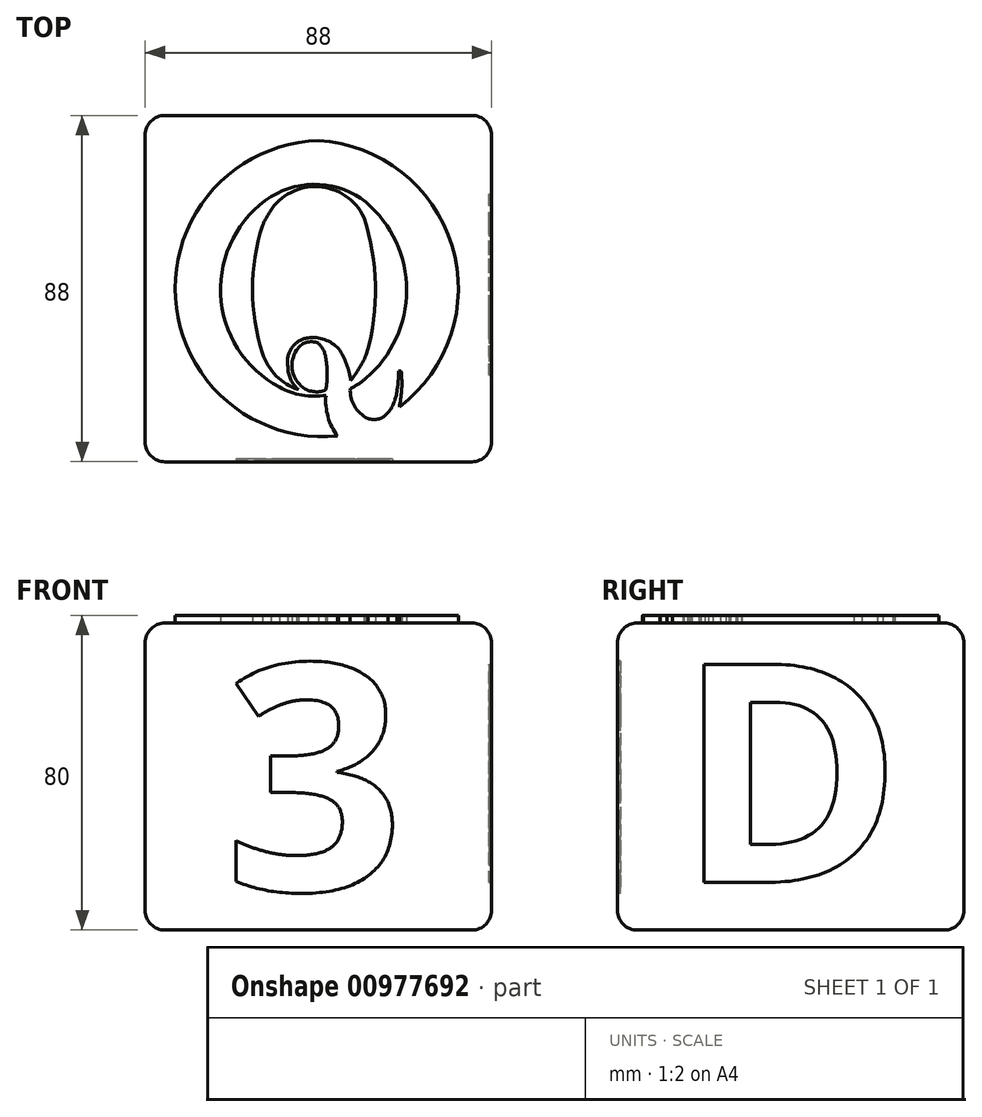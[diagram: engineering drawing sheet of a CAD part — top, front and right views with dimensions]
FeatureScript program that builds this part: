
annotation { "Feature Type Name" : "Feature", "Feature Type Description" : "" }
export const myFeature = defineFeature(function(context is Context, id is Id, definition is map)
    precondition{}
    {
        {
            var Q0;
            Q0=qCreatedBy(makeId("Top.planeOp"),FACE);
            var sketch = newSketch(context, id + "F0", { "sketchPlane" : qUnion([Q0])});
            skPoint(sketch, "E0.first.point", {"position": v(-8.97, 42.4) * mm});
            skPoint(sketch, "E0.second.point", {"position": v(4.84, -31.38) * mm});
            skPoint(sketch, "E0.third.point", {"position": v(40.23, 13.72) * mm});
            skArc(sketch, "E1", {"start": v(0, 43.7) * mm, "mid": v(-36.34, 3.66) * mm, "end": v(4.84, -31.38) * mm});
            skArc(sketch, "E2", {"start": v(20.57, -24) * mm, "mid": v(33.91, 17.02) * mm, "end": v(0, 43.7) * mm});
            skArc(sketch, "E3", {"start": v(-12, 29.47) * mm, "mid": v(-24.84, 4.65) * mm, "end": v(-9.87, -18.96) * mm});
            skArc(sketch, "E4", {"start": v(12.09, 28.05) * mm, "mid": v(0.27, 32.56) * mm, "end": v(-12, 29.47) * mm});
            skArc(sketch, "E5", {"start": v(12.09, -16.68) * mm, "mid": v(22.4, 5.68) * mm, "end": v(12.09, 28.05) * mm});
            skArc(sketch, "E6", {"start": v(8.11, -19.25) * mm, "mid": v(10.22, -18.15) * mm, "end": v(12.09, -16.68) * mm});
            skArc(sketch, "E7", {"start": v(-9.87, -18.96) * mm, "mid": v(-4.16, -21) * mm, "end": v(1.9, -21.05) * mm});
            skArc(sketch, "E8", {"start": v(1.9, -21.05) * mm, "mid": v(2.44, -26.48) * mm, "end": v(4.84, -31.38) * mm});
            skArc(sketch, "E9", {"start": v(8.11, -19.25) * mm, "mid": v(9.16, -23.77) * mm, "end": v(12.57, -26.92) * mm});
            skArc(sketch, "E10", {"start": v(12.57, -26.92) * mm, "mid": v(15.38, -27) * mm, "end": v(17.7, -25.42) * mm});
            skArc(sketch, "E11", {"start": v(17.7, -25.42) * mm, "mid": v(19.27, -22.75) * mm, "end": v(19.99, -19.74) * mm});
            skArc(sketch, "E12", {"start": v(19.99, -19.74) * mm, "mid": v(20.3, -17.3) * mm, "end": v(20.33, -14.85) * mm});
            skLineSegment(sketch, "E13", {"start": v(20.33, -14.85) * mm, "end": v(21.05, -14.85) * mm});
            skArc(sketch, "E14", {"start": v(20.57, -24) * mm, "mid": v(21.16, -19.45) * mm, "end": v(21.05, -14.85) * mm});
            skArc(sketch, "E15", {"start": v(11.56, 24.17) * mm, "mid": v(0.05, 31.98) * mm, "end": v(-12.33, 25.65) * mm});
            skArc(sketch, "E16", {"start": v(-12.33, 25.65) * mm, "mid": v(-13.33, 23.93) * mm, "end": v(-14.2, 22.14) * mm});
            skArc(sketch, "E17", {"start": v(12.27, -10.4) * mm, "mid": v(14.51, 6.94) * mm, "end": v(11.56, 24.17) * mm});
            skArc(sketch, "E18", {"start": v(8.2, -17.28) * mm, "mid": v(10.48, -13.99) * mm, "end": v(12.27, -10.4) * mm});
            skArc(sketch, "E19", {"start": v(-14.2, 22.14) * mm, "mid": v(-16.74, 5.87) * mm, "end": v(-14.2, -10.4) * mm});
            skArc(sketch, "E20", {"start": v(-14.2, -10.4) * mm, "mid": v(-10.74, -16.1) * mm, "end": v(-5.08, -19.62) * mm});
            skArc(sketch, "E21.trimOffspring", {"start": v(21.12, -15.68) * mm, "mid": v(21.07, -15.26) * mm, "end": v(21.03, -14.85) * mm});
            skArc(sketch, "E22", {"start": v(-7.75, -13.7) * mm, "mid": v(-7.09, -16.96) * mm, "end": v(-5.08, -19.62) * mm});
            skArc(sketch, "E23", {"start": v(-2.67, -6.43) * mm, "mid": v(-6.77, -8.98) * mm, "end": v(-7.75, -13.7) * mm});
            skArc(sketch, "E24", {"start": v(5.17, -9.2) * mm, "mid": v(1.57, -6.89) * mm, "end": v(-2.67, -6.43) * mm});
            skArc(sketch, "E25", {"start": v(8.2, -17.28) * mm, "mid": v(7.13, -13.07) * mm, "end": v(5.17, -9.2) * mm});
            skArc(sketch, "E26", {"start": v(1.9, -19.62) * mm, "mid": v(2.22, -15.67) * mm, "end": v(1.9, -11.72) * mm});
            skArc(sketch, "E27", {"start": v(1.9, -11.72) * mm, "mid": v(1.3, -9.59) * mm, "end": v(0, -7.8) * mm});
            skArc(sketch, "E28", {"start": v(0, -7.8) * mm, "mid": v(-3.12, -7.64) * mm, "end": v(-5.56, -9.59) * mm});
            skPoint(sketch, "E28.endSnap0", {"position": v(1.3, -9.59) * mm});
            skArc(sketch, "E29", {"start": v(-5.56, -9.59) * mm, "mid": v(-6.65, -14.33) * mm, "end": v(-4.4, -18.65) * mm});
            skArc(sketch, "E30", {"start": v(-4.4, -18.65) * mm, "mid": v(-1.39, -20.08) * mm, "end": v(1.9, -19.62) * mm});
            skSolve(sketch);
        }
        {
            var Q0;
            Q0 = qSketchRegion(id + "F0", true);
            extrude(context, id + "F1", {"entities" : qUnion([Q0]), "depth" : 25 * mm, "offsetDistance" : 25 * mm});
        }
        {
            var Q0;
            Q0=makeQuery(id+"F1.opExtrude","CAP_FACE",FACE,{"disambiguationData":[OSD([sQuery(id+"F0.wireOp",EDGE,"E1"),sQuery(id+"F0.wireOp",EDGE,"E2"),sQuery(id+"F0.wireOp",EDGE,"E3"),sQuery(id+"F0.wireOp",EDGE,"E4"),sQuery(id+"F0.wireOp",EDGE,"E5"),sQuery(id+"F0.wireOp",EDGE,"E6"),sQuery(id+"F0.wireOp",EDGE,"E7"),sQuery(id+"F0.wireOp",EDGE,"E8"),sQuery(id+"F0.wireOp",EDGE,"E9"),sQuery(id+"F0.wireOp",EDGE,"E10"),sQuery(id+"F0.wireOp",EDGE,"E11"),sQuery(id+"F0.wireOp",EDGE,"E12"),sQuery(id+"F0.wireOp",EDGE,"E13"),sQuery(id+"F0.wireOp",EDGE,"E14"),sQuery(id+"F0.wireOp",EDGE,"E21.trimOffspring")])],"isStart":true});
            var sketch = newSketch(context, id + "F2", { "sketchPlane" : qUnion([Q0])});
            skArc(sketch, "E31", {"start": v(0, -43.7) * mm, "mid": v(35.47, -8.29) * mm, "end": v(4.84, 31.38) * mm});
            skArc(sketch, "E32", {"start": v(4.84, 31.38) * mm, "mid": v(-36.41, -3.65) * mm, "end": v(0, -43.7) * mm});
            skSolve(sketch);
        }
        {
            var Q0;
            Q0=qCreatedBy(makeId("Top.planeOp"),FACE);
            var sketch = newSketch(context, id + "F3", { "sketchPlane" : qUnion([Q0])});
            skLineSegment(sketch, "E33.top", {"start": v(39, -37.91) * mm, "end": v(-39, -37.91) * mm});
            skLineSegment(sketch, "E33.left", {"start": v(44, 45.09) * mm, "end": v(44, -32.91) * mm});
            skLineSegment(sketch, "E33.right", {"start": v(-44, 45.09) * mm, "end": v(-44, -32.91) * mm});
            skPoint(sketch, "E33.middle", {"position": v(0, 0) * mm});
            skPoint(sketch, "E34.visualSharp", {"position": v(-44, 37.91) * mm});
            skPoint(sketch, "E35.visualSharp", {"position": v(44, 37.91) * mm});
            skLineSegment(sketch, "E36", {"start": v(-39, 50.09) * mm, "end": v(39, 50.09) * mm});
            skPoint(sketch, "E37.visualSharp", {"position": v(-44, 50.09) * mm});
            skArc(sketch, "E37.filletArc", {"start": v(-39, 50.09) * mm, "mid": v(-42.54, 48.62) * mm, "end": v(-44, 45.09) * mm});
            skPoint(sketch, "E38.visualSharp", {"position": v(44, 50.09) * mm});
            skArc(sketch, "E38.filletArc", {"start": v(44, 45.09) * mm, "mid": v(42.54, 48.62) * mm, "end": v(39, 50.09) * mm});
            skPoint(sketch, "E39.visualSharp", {"position": v(44, -37.91) * mm});
            skArc(sketch, "E39.filletArc", {"start": v(39, -37.91) * mm, "mid": v(42.54, -36.45) * mm, "end": v(44, -32.91) * mm});
            skPoint(sketch, "E40.visualSharp", {"position": v(-44, -37.91) * mm});
            skArc(sketch, "E40.filletArc", {"start": v(-44, -32.91) * mm, "mid": v(-42.54, -36.45) * mm, "end": v(-39, -37.91) * mm});
            skSolve(sketch);
        }
        {
            var Q0;
            Q0 = qSketchRegion(id + "F3", true);
            extrude(context, id + "F4", {"entities" : qUnion([Q0]), "operationType" : NewBodyOperationType.ADD, "oppositeDirection" : true, "depth" : 55 * mm, "offsetDistance" : 25 * mm, "hasSecondDirection" : true, "secondDirectionOppositeDirection" : false, "secondDirectionDepth" : 23 * mm});
        }
        {
            var Q0;
            Q0=makeQuery(id+"F4.opExtrude","SWEPT_FACE",FACE,{"disambiguationData":[OSD([sQuery(id+"F3.wireOp",EDGE,"E33.left")])]});
            var sketch = newSketch(context, id + "F5", { "sketchPlane" : qUnion([Q0])});
            skText(sketch, "E41", { "text": "D", "fontName": "OpenSans-Bold.ttf"});
            const initialGuessF5  = {"E41": [-0.02291, -0.0429, 1, 0, 0.0559]};
            skSetInitialGuess(sketch, initialGuessF5);
            skSolve(sketch);
        }
        {
            var Q0;
            Q0 = qSketchRegion(id + "F5", true);
            extrude(context, id + "F6", {"entities" : qUnion([Q0]), "operationType" : NewBodyOperationType.REMOVE, "oppositeDirection" : true, "depth" : 0.7 * mm, "offsetDistance" : 25 * mm});
        }
        {
            var Q0;
            Q0=makeQuery(id+"F4.opExtrude","SWEPT_FACE",FACE,{"disambiguationData":[OSD([sQuery(id+"F3.wireOp",EDGE,"E33.top")])]});
            var sketch = newSketch(context, id + "F7", { "sketchPlane" : qUnion([Q0])});
            skText(sketch, "E42", { "text": "3", "fontName": "OpenSans-Bold.ttf"});
            const initialGuessF7  = {"E42": [-0.024, -0.04489, 1, 0, 0.05789]};
            skSetInitialGuess(sketch, initialGuessF7);
            skSolve(sketch);
        }
        {
            var Q0;
            Q0 = qSketchRegion(id + "F7", true);
            extrude(context, id + "F8", {"entities" : qUnion([Q0]), "operationType" : NewBodyOperationType.REMOVE, "oppositeDirection" : true, "depth" : 0.7 * mm, "offsetDistance" : 25 * mm});
        }
        {
            var Q0;
            Q0=makeQuery(id+"F4.opExtrude","CAP_EDGE",EDGE,{"disambiguationData":[OSD([sQuery(id+"F3.wireOp",EDGE,"E33.top")])],"isStart":true});
            var Q1;
            Q1=makeQuery(id+"F4.opExtrude","CAP_FACE",FACE,{"disambiguationData":[OSD([sQuery(id+"F3.wireOp",EDGE,"E33.top"),sQuery(id+"F3.wireOp",EDGE,"E33.left"),sQuery(id+"F3.wireOp",EDGE,"E33.right"),sQuery(id+"F3.wireOp",EDGE,"E36"),sQuery(id+"F3.wireOp",EDGE,"E37.filletArc"),sQuery(id+"F3.wireOp",EDGE,"E38.filletArc"),sQuery(id+"F3.wireOp",EDGE,"E39.filletArc"),sQuery(id+"F3.wireOp",EDGE,"E40.filletArc")])],"isStart":false});
            fillet(context, id + "F9", {"entities" : qUnion([Q0, Q1]), "radius" : 5 * mm, "tangentPropagation" : true, "allowEdgeOverflow" : false});
        }
    });
